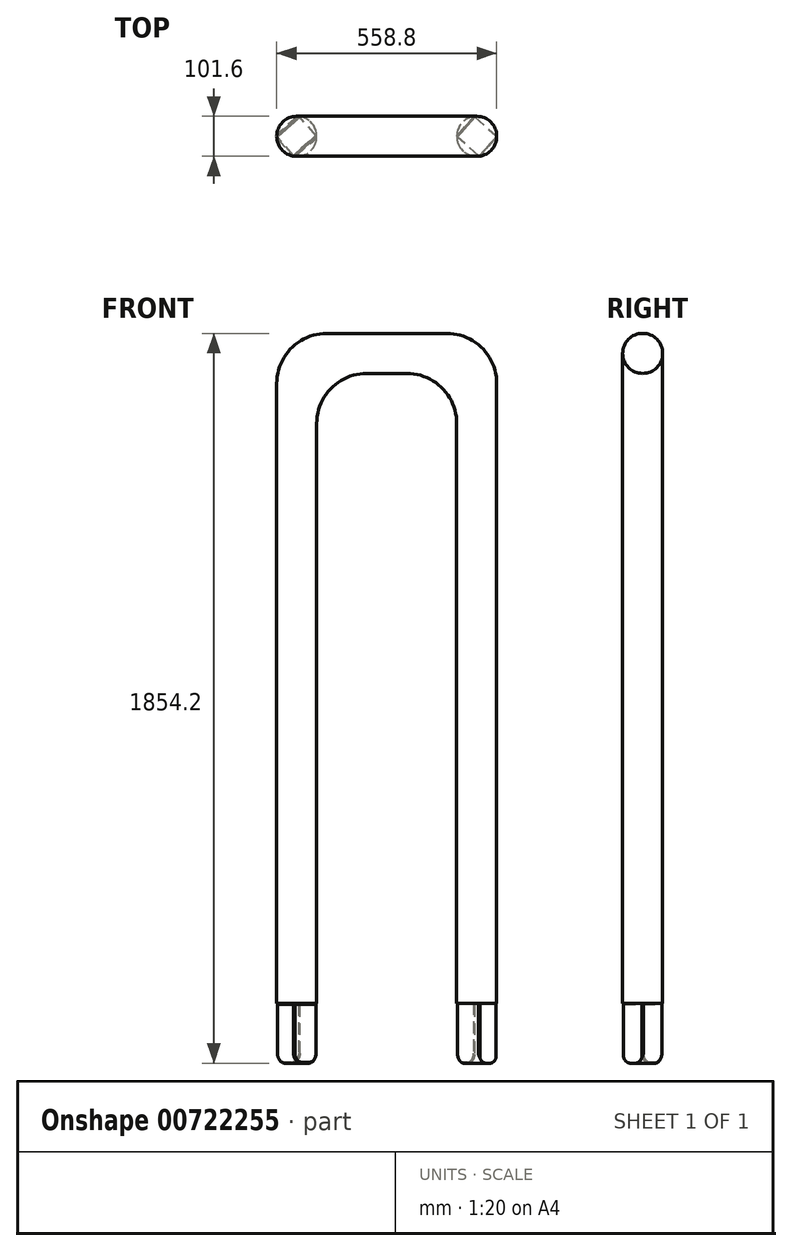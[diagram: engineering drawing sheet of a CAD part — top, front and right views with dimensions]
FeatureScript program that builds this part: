
annotation { "Feature Type Name" : "Feature", "Feature Type Description" : "" }
export const myFeature = defineFeature(function(context is Context, id is Id, definition is map)
    precondition{}
    {
        {
            var Q0;
            Q0=qCreatedBy(makeId("Front.planeOp"),FACE);
            var sketch = newSketch(context, id + "F0", { "sketchPlane" : qUnion([Q0])});
            skLineSegment(sketch, "E0", {"start": v(-279.4, 101.6) * mm, "end": v(0, 101.6) * mm});
            skLineSegment(sketch, "E1", {"start": v(279.4, 101.6) * mm, "end": v(279.4, -787.4) * mm});
            skLineSegment(sketch, "E2", {"start": v(279.4, -787.4) * mm, "end": v(177.8, -787.4) * mm});
            skLineSegment(sketch, "E3", {"start": v(177.8, -787.4) * mm, "end": v(177.8, 0) * mm});
            skLineSegment(sketch, "E4", {"start": v(177.8, 0) * mm, "end": v(-177.8, 0) * mm});
            skLineSegment(sketch, "E5", {"start": v(-177.8, 0) * mm, "end": v(-177.8, -787.4) * mm});
            skLineSegment(sketch, "E6", {"start": v(-177.8, -787.4) * mm, "end": v(-279.4, -787.4) * mm});
            skLineSegment(sketch, "E7", {"start": v(-279.4, -787.4) * mm, "end": v(-279.4, 101.6) * mm});
            skLineSegment(sketch, "E8", {"start": v(0, 101.6) * mm, "end": v(0, 0) * mm, "construction": true});
            skLineSegment(sketch, "E9", {"start": v(0, 101.6) * mm, "end": v(279.4, 101.6) * mm});
            skPoint(sketch, "E10", {"position": v(0, 0) * mm});
            skSolve(sketch);
        }
        {
            var Q0;
            Q0=makeQuery(id+"F0.imprint","IMPRINT",FACE,{"disambiguationData":[TD([[makeQuery(id+"F0.imprint","IMPRINT",EDGE,{"derivedFrom":sQuery(id+"F0.wireOp",EDGE,"E0")}),-1.0]])]});
            extrude(context, id + "F1", {"entities" : qUnion([Q0]), "depth" : 101.6 * mm, "offsetDistance" : 25.4 * mm});
        }
        {
            var Q0;
            Q0=makeQuery(id+"F1.opExtrude","SWEPT_EDGE",EDGE,{"disambiguationData":[OSD([sQuery(id+"F0.wireOp",EDGE,"E4"),sQuery(id+"F0.wireOp",EDGE,"E5")])]});
            fillet(context, id + "F2", {"entities" : qUnion([Q0]), "radius" : 127 * mm, "tangentPropagation" : true, "allowEdgeOverflow" : false});
        }
        {
            var Q0;
            Q0=makeQuery(id+"F1.opExtrude","SWEPT_EDGE",EDGE,{"disambiguationData":[OSD([sQuery(id+"F0.wireOp",EDGE,"E3"),sQuery(id+"F0.wireOp",EDGE,"E4")])]});
            fillet(context, id + "F3", {"entities" : qUnion([Q0]), "radius" : 127 * mm, "tangentPropagation" : true, "allowEdgeOverflow" : false});
        }
        {
            var Q0;
            Q0=makeQuery(id+"F1.opExtrude","SWEPT_EDGE",EDGE,{"disambiguationData":[OSD([sQuery(id+"F0.wireOp",EDGE,"E0"),sQuery(id+"F0.wireOp",EDGE,"E7")])]});
            fillet(context, id + "F4", {"entities" : qUnion([Q0]), "radius" : 127 * mm, "tangentPropagation" : true, "allowEdgeOverflow" : false});
        }
        {
            var Q0;
            Q0=makeQuery(id+"F1.opExtrude","SWEPT_EDGE",EDGE,{"disambiguationData":[OSD([sQuery(id+"F0.wireOp",EDGE,"E1"),sQuery(id+"F0.wireOp",EDGE,"E9")])]});
            fillet(context, id + "F5", {"entities" : qUnion([Q0]), "radius" : 127 * mm, "tangentPropagation" : true, "allowEdgeOverflow" : false});
        }
        {
            var Q0;
            Q0=makeQuery(id+"F1.opExtrude","CAP_EDGE",EDGE,{"disambiguationData":[OSD([sQuery(id+"F0.wireOp",EDGE,"E1")])],"isStart":true});
            var Q1;
            Q1=makeQuery(id+"F1.opExtrude","CAP_EDGE",EDGE,{"disambiguationData":[OSD([sQuery(id+"F0.wireOp",EDGE,"E3")])],"isStart":true});
            var Q2;
            Q2=makeQuery(id+"F1.opExtrude","CAP_EDGE",EDGE,{"disambiguationData":[OSD([sQuery(id+"F0.wireOp",EDGE,"E1")])],"isStart":false});
            var Q3;
            Q3=makeQuery(id+"F1.opExtrude","CAP_EDGE",EDGE,{"disambiguationData":[OSD([sQuery(id+"F0.wireOp",EDGE,"E3")])],"isStart":false});
            fillet(context, id + "F6", {"entities" : qUnion([Q0, Q1, Q2, Q3]), "radius" : 50.8 * mm, "tangentPropagation" : true, "allowEdgeOverflow" : false});
        }
        {
            var Q0;
            Q0=makeQuery(id+"F1.opExtrude","SWEPT_FACE",FACE,{"disambiguationData":[OSD([sQuery(id+"F0.wireOp",EDGE,"E6")])]});
            var Q1;
            Q1=makeQuery(id+"F1.opExtrude","SWEPT_FACE",FACE,{"disambiguationData":[OSD([sQuery(id+"F0.wireOp",EDGE,"E2")])]});
            extrude(context, id + "F7", {"entities" : qUnion([Q0, Q1]), "operationType" : NewBodyOperationType.ADD, "depth" : 812.8 * mm, "offsetDistance" : 25.4 * mm});
        }
        {
            var Q0;
            Q0=makeQuery(id+"F7.opExtrude","CAP_FACE",FACE,{"disambiguationData":[OSD([sQuery(id+"F0.wireOp",EDGE,"E6")])],"isStart":false});
            var sketch = newSketch(context, id + "F8", { "sketchPlane" : qUnion([Q0])});
            skPoint(sketch, "E11", {"position": v(-228.6, 50.8) * mm});
            skLineSegment(sketch, "E12", {"start": v(-222.25, 0.4) * mm, "end": v(-279.4, 50.8) * mm});
            skLineSegment(sketch, "E13", {"start": v(-279.4, 50.8) * mm, "end": v(-234.95, 101.2) * mm});
            skLineSegment(sketch, "E14", {"start": v(-234.95, 101.2) * mm, "end": v(-177.8, 50.8) * mm});
            skLineSegment(sketch, "E15", {"start": v(-177.8, 50.8) * mm, "end": v(-222.25, 0.4) * mm});
            skCircle(sketch, "E16.0", {"center": v(-228.6, 50.8) * mm, "radius": 50.8 * mm});
            skPoint(sketch, "E17", {"position": v(228.6, 50.8) * mm});
            skLineSegment(sketch, "E18", {"start": v(228.6, 50.8) * mm, "end": v(-228.6, 50.8) * mm, "construction": true});
            skLineSegment(sketch, "E19", {"start": v(-222.25, 0.4) * mm, "end": v(-228.6, 50.8) * mm, "construction": true});
            skPoint(sketch, "E20", {"position": v(0, 50.8) * mm});
            skLineSegment(sketch, "E21", {"start": v(0, 207.37) * mm, "end": v(0, -184.62) * mm, "construction": true});
            skLineSegment(sketch, "E22.MirrorCS", {"start": v(234.95, 101.2) * mm, "end": v(177.8, 50.8) * mm});
            skLineSegment(sketch, "E23.MirrorCS", {"start": v(279.4, 50.8) * mm, "end": v(234.95, 101.2) * mm});
            skLineSegment(sketch, "E24.MirrorCS", {"start": v(222.25, 0.4) * mm, "end": v(279.4, 50.8) * mm});
            skLineSegment(sketch, "E25.MirrorCS", {"start": v(177.8, 50.8) * mm, "end": v(222.25, 0.4) * mm});
            skSolve(sketch);
        }
        {
            var Q0;
            Q0=makeQuery(id+"F8.imprint","IMPRINT",FACE,{"disambiguationData":[TD([[makeQuery(id+"F8.imprint","IMPRINT",EDGE,{"derivedFrom":sQuery(id+"F8.wireOp",EDGE,"E12")}),-1.0]])]});
            var Q1;
            Q1=sQuery(id+"F8.wireOp",EDGE,"E13");
            var Q2;
            Q2=sQuery(id+"F8.wireOp",EDGE,"E12");
            var Q3;
            Q3=sQuery(id+"F8.wireOp",EDGE,"E15");
            var Q4;
            Q4=sQuery(id+"F8.wireOp",EDGE,"E14");
            extrude(context, id + "F9", {"entities" : qUnion([Q0]), "operationType" : NewBodyOperationType.ADD, "surfaceEntities" : qUnion([Q1, Q2, Q3, Q4]), "depth" : 152.4 * mm, "offsetDistance" : 25.4 * mm});
        }
        {
            var Q0;
            Q0=makeQuery(id+"F9.opExtrude","CAP_EDGE",EDGE,{"disambiguationData":[OSD([sQuery(id+"F8.wireOp",EDGE,"E15")])],"isStart":false});
            var Q1;
            Q1=makeQuery(id+"F9.opExtrude","CAP_EDGE",EDGE,{"disambiguationData":[OSD([sQuery(id+"F8.wireOp",EDGE,"E13")])],"isStart":false});
            fillet(context, id + "F10", {"entities" : qUnion([Q0, Q1]), "radius" : 25.4 * mm, "tangentPropagation" : true, "allowEdgeOverflow" : false});
        }
        {
            var Q0;
            Q0=makeQuery(id+"F9.opExtrude","SWEPT_EDGE",EDGE,{"disambiguationData":[OSD([sQuery(id+"F8.wireOp",EDGE,"E13"),sQuery(id+"F8.wireOp",EDGE,"E14"),sQuery(id+"F8.wireOp",EDGE,"E16.0")])]});
            var Q1;
            Q1=makeQuery(id+"F9.opExtrude","SWEPT_EDGE",EDGE,{"disambiguationData":[OSD([sQuery(id+"F8.wireOp",EDGE,"E12"),sQuery(id+"F8.wireOp",EDGE,"E13"),sQuery(id+"F8.wireOp",EDGE,"E16.0")])]});
            chamfer(context, id + "F11", {"entities" : qUnion([Q0, Q1]), "width" : 2.54 * mm, "tangentPropagation" : true});
        }
        {
            var Q0;
            Q0=makeQuery(id+"F9.opExtrude","CAP_EDGE",EDGE,{"disambiguationData":[OSD([sQuery(id+"F8.wireOp",EDGE,"E15")])],"isStart":true});
            var Q1;
            Q1=makeQuery(id+"F9.opExtrude","CAP_EDGE",EDGE,{"disambiguationData":[OSD([sQuery(id+"F8.wireOp",EDGE,"E14")])],"isStart":true});
            var Q2;
            Q2=makeQuery(id+"F9.opExtrude","CAP_EDGE",EDGE,{"disambiguationData":[OSD([sQuery(id+"F8.wireOp",EDGE,"E12")])],"isStart":true});
            var Q3;
            Q3=makeQuery(id+"F9.opExtrude","CAP_EDGE",EDGE,{"disambiguationData":[OSD([sQuery(id+"F8.wireOp",EDGE,"E13")])],"isStart":true});
            chamfer(context, id + "F12", {"entities" : qUnion([Q0, Q1, Q2, Q3]), "width" : 2.54 * mm, "tangentPropagation" : true});
        }
        {
            var Q0;
            Q0=makeQuery(id+"F8.imprint","IMPRINT",FACE,{"disambiguationData":[TD([[makeQuery(id+"F8.imprint","IMPRINT",EDGE,{"derivedFrom":sQuery(id+"F8.wireOp",EDGE,"E22.MirrorCS")}),1.0]])]});
            extrude(context, id + "F13", {"entities" : qUnion([Q0]), "operationType" : NewBodyOperationType.ADD, "depth" : 152.4 * mm, "offsetDistance" : 25.4 * mm});
        }
        {
            var Q0;
            Q0=makeQuery(id+"F13.opExtrude","SWEPT_EDGE",EDGE,{"disambiguationData":[OSD([sQuery(id+"F8.wireOp",EDGE,"E22.MirrorCS"),sQuery(id+"F8.wireOp",EDGE,"E23.MirrorCS")])]});
            var Q1;
            Q1=makeQuery(id+"F13.opExtrude","SWEPT_EDGE",EDGE,{"disambiguationData":[OSD([sQuery(id+"F8.wireOp",EDGE,"E23.MirrorCS"),sQuery(id+"F8.wireOp",EDGE,"E24.MirrorCS")])]});
            chamfer(context, id + "F14", {"entities" : qUnion([Q0, Q1]), "width" : 2.54 * mm, "tangentPropagation" : true});
        }
        {
            var Q0;
            Q0=makeQuery(id+"F13.opExtrude","CAP_EDGE",EDGE,{"disambiguationData":[OSD([sQuery(id+"F8.wireOp",EDGE,"E22.MirrorCS")])],"isStart":false});
            var Q1;
            Q1=makeQuery(id+"F13.opExtrude","CAP_EDGE",EDGE,{"disambiguationData":[OSD([sQuery(id+"F8.wireOp",EDGE,"E24.MirrorCS")])],"isStart":false});
            fillet(context, id + "F15", {"entities" : qUnion([Q0, Q1]), "radius" : 25.4 * mm, "tangentPropagation" : true, "allowEdgeOverflow" : false});
        }
        {
            var Q0;
            Q0=makeQuery(id+"F13.opExtrude","SWEPT_EDGE",EDGE,{"disambiguationData":[OSD([sQuery(id+"F8.wireOp",EDGE,"E24.MirrorCS"),sQuery(id+"F8.wireOp",EDGE,"E25.MirrorCS")])]});
            chamfer(context, id + "F16", {"entities" : qUnion([Q0]), "width" : 2.54 * mm, "tangentPropagation" : true});
        }
    });
